# Revit family: QF_LANCER_IBD 4500-25_cat
name_source: partatom
category: Specialty Equipment
revit_build: Autodesk Revit Architecture 2012 (Build: 20110916_2132(x64)
units: mm (PartAtom-declared; Revit-internal decimal feet)

## types (1)
- QF_LANCER_IBD 4500-25_cat
    Apparent Power = 345 VA
    Cold Water Connection Height = 0"
    Cold Water Flow = 0 GPM
    Cold Water Maximum Pressure = 0.00 psi
    Cold Water Minimum Pressure = 0.00 psi
    Cold Water RI Height = 0"
    Cold Water Size = 0"
    Cold Water Temperature Recommended = -460 °F
    Conn Conduit = Yes
    Cycle = 60 Hz
    Description = ICE BEVERAGE DISPENSER
    FL Amps = 3 A
    Indirect Waste Connection Height = 0"
    Indirect Waste Flow = 0 GPM
    Indirect Waste Size = 1"
    Manufacturer = LANCER
    Max Overcurrent Protection = 0 A
    Min Ckt Ampacity = 0 A
    Model = IBD 4500-25
    Phase = 0
    URL = www.lancercorp.com
    URL Cutsheet = www.lancercorp.com
    Volts = 115 V
    Waste Water Discharge Temperature = -460 °F
    Watts = 0 W
    Weight in Pounds = 0

## geometry (parser evidence)
native form markers: Blend x7, Sweep x5
no freeform markers — native parametric forms only
